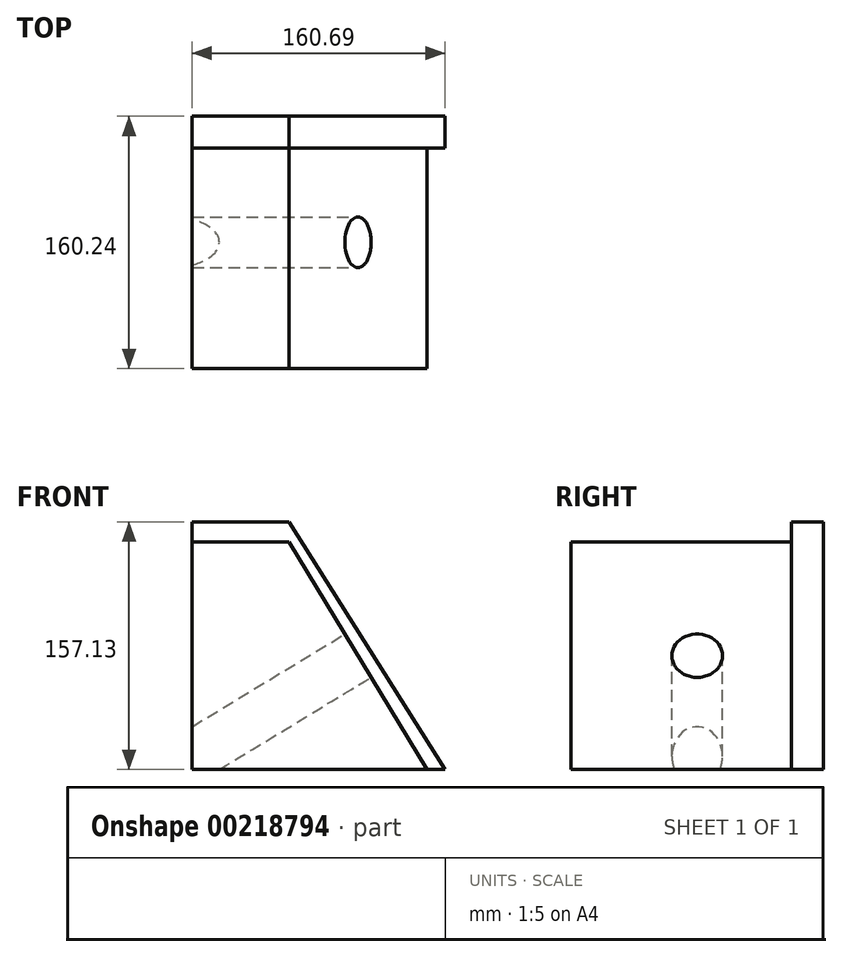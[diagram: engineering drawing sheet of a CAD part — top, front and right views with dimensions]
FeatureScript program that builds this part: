
annotation { "Feature Type Name" : "Feature", "Feature Type Description" : "" }
export const myFeature = defineFeature(function(context is Context, id is Id, definition is map)
    precondition{}
    {
        {
            var Q0;
            Q0=qCreatedBy(makeId("Top.planeOp"),FACE);
            var sketch = newSketch(context, id + "F0", { "sketchPlane" : qUnion([Q0])});
            skLineSegment(sketch, "E0.bottom", {"start": v(-90.86, 80.12) * mm, "end": v(90.86, 80.12) * mm});
            skLineSegment(sketch, "E0.top", {"start": v(-90.86, -80.12) * mm, "end": v(90.86, -80.12) * mm});
            skLineSegment(sketch, "E0.left", {"start": v(-90.86, 80.12) * mm, "end": v(-90.86, -80.12) * mm});
            skLineSegment(sketch, "E0.right", {"start": v(90.86, 80.12) * mm, "end": v(90.86, -80.12) * mm});
            skPoint(sketch, "E0.middle", {"position": v(0, 0) * mm});
            skSolve(sketch);
        }
        {
            var Q0;
            Q0 = qSketchRegion(id + "F0", true);
            extrude(context, id + "F1", {"entities" : qUnion([Q0]), "depth" : 144.27 * mm});
        }
        {
            var Q0;
            Q0=makeQuery(id+"F1.opExtrude","SWEPT_FACE",FACE,{"disambiguationData":[OSD([sQuery(id+"F0.wireOp",EDGE,"E0.top")])]});
            var sketch = newSketch(context, id + "F2", { "sketchPlane" : qUnion([Q0])});
            skLineSegment(sketch, "E1", {"start": v(-42.42, 166.15) * mm, "end": v(62.8, -7.55) * mm});
            skLineSegment(sketch, "E2", {"start": v(62.8, -7.55) * mm, "end": v(116.58, -7.55) * mm});
            skLineSegment(sketch, "E3", {"start": v(-42.42, 166.15) * mm, "end": v(116.58, 147.11) * mm});
            skLineSegment(sketch, "E4", {"start": v(116.58, 147.11) * mm, "end": v(116.58, -7.55) * mm});
            skSolve(sketch);
        }
        {
            var Q0;
            {var subQ1=sQuery(id+"F0.wireOp",EDGE,"E0.top");var subQ6=makeQuery(id+"F1.opExtrude","SWEPT_EDGE",EDGE,{"disambiguationData":[OSD([subQ1,sQuery(id+"F0.wireOp",EDGE,"E0.right")])]});Q0=makeQuery(id+"F2.imprint","IMPRINT",FACE,{"disambiguationData":[TD([[makeQuery(id+"F2.imprint","IMPRINT",EDGE,{"derivedFrom":subQ6}),-1.0]])]});}
            extrude(context, id + "F3", {"entities" : qUnion([Q0]), "operationType" : NewBodyOperationType.REMOVE, "endBound" : BoundingType.UP_TO_NEXT, "oppositeDirection" : true, "depth" : 25.4 * mm});
        }
        {
            var Q0;
            Q0=makeQuery(id+"F3.boolean.opBoolean","COPY",FACE,{"derivedFrom":makeQuery(id+"F3.opExtrude","SWEPT_FACE",FACE,{"disambiguationData":[OSD([sQuery(id+"F2.wireOp",EDGE,"E1")])]})});
            var sketch = newSketch(context, id + "F4", { "sketchPlane" : qUnion([Q0])});
            skCircle(sketch, "E5", {"center": v(0, 54.17) * mm, "radius": 16.07 * mm});
            skPoint(sketch, "E5.centerSnap0", {"position": v(-80.12, 54.17) * mm});
            skPoint(sketch, "E5.centerSnap1", {"position": v(0, 138.51) * mm});
            skSolve(sketch);
        }
        {
            var Q0;
            Q0 = qSketchRegion(id + "F4", true);
            extrude(context, id + "F5", {"entities" : qUnion([Q0]), "operationType" : NewBodyOperationType.REMOVE, "endBound" : BoundingType.UP_TO_NEXT, "oppositeDirection" : true, "depth" : 25.4 * mm});
        }
        {
            var Q0;
            Q0=makeQuery(id+"F1.opExtrude","SWEPT_FACE",FACE,{"disambiguationData":[OSD([sQuery(id+"F0.wireOp",EDGE,"E0.bottom")])]});
            var sketch = newSketch(context, id + "F6", { "sketchPlane" : qUnion([Q0])});
            skLineSegment(sketch, "E6", {"start": v(90.86, 144.27) * mm, "end": v(90.86, 157.13) * mm});
            skLineSegment(sketch, "E7", {"start": v(90.86, 157.13) * mm, "end": v(29.17, 157.13) * mm});
            skLineSegment(sketch, "E8", {"start": v(29.17, 157.13) * mm, "end": v(-69.83, 0) * mm});
            skLineSegment(sketch, "E9", {"start": v(-69.83, 0) * mm, "end": v(-58.23, 0) * mm});
            skLineSegment(sketch, "E10", {"start": v(-58.23, 0) * mm, "end": v(29.17, 144.27) * mm});
            skLineSegment(sketch, "E11", {"start": v(29.17, 144.27) * mm, "end": v(90.86, 144.27) * mm});
            skSolve(sketch);
        }
        {
            var Q0;
            Q0=makeQuery(id+"F6.imprint","IMPRINT",FACE,{"disambiguationData":[TD([[makeQuery(id+"F6.imprint","IMPRINT",EDGE,{"derivedFrom":sQuery(id+"F6.wireOp",EDGE,"E6")}),1.0]])]});
            extrude(context, id + "F7", {"entities" : qUnion([Q0]), "operationType" : NewBodyOperationType.ADD, "oppositeDirection" : true, "depth" : 20.32 * mm});
        }
    });
